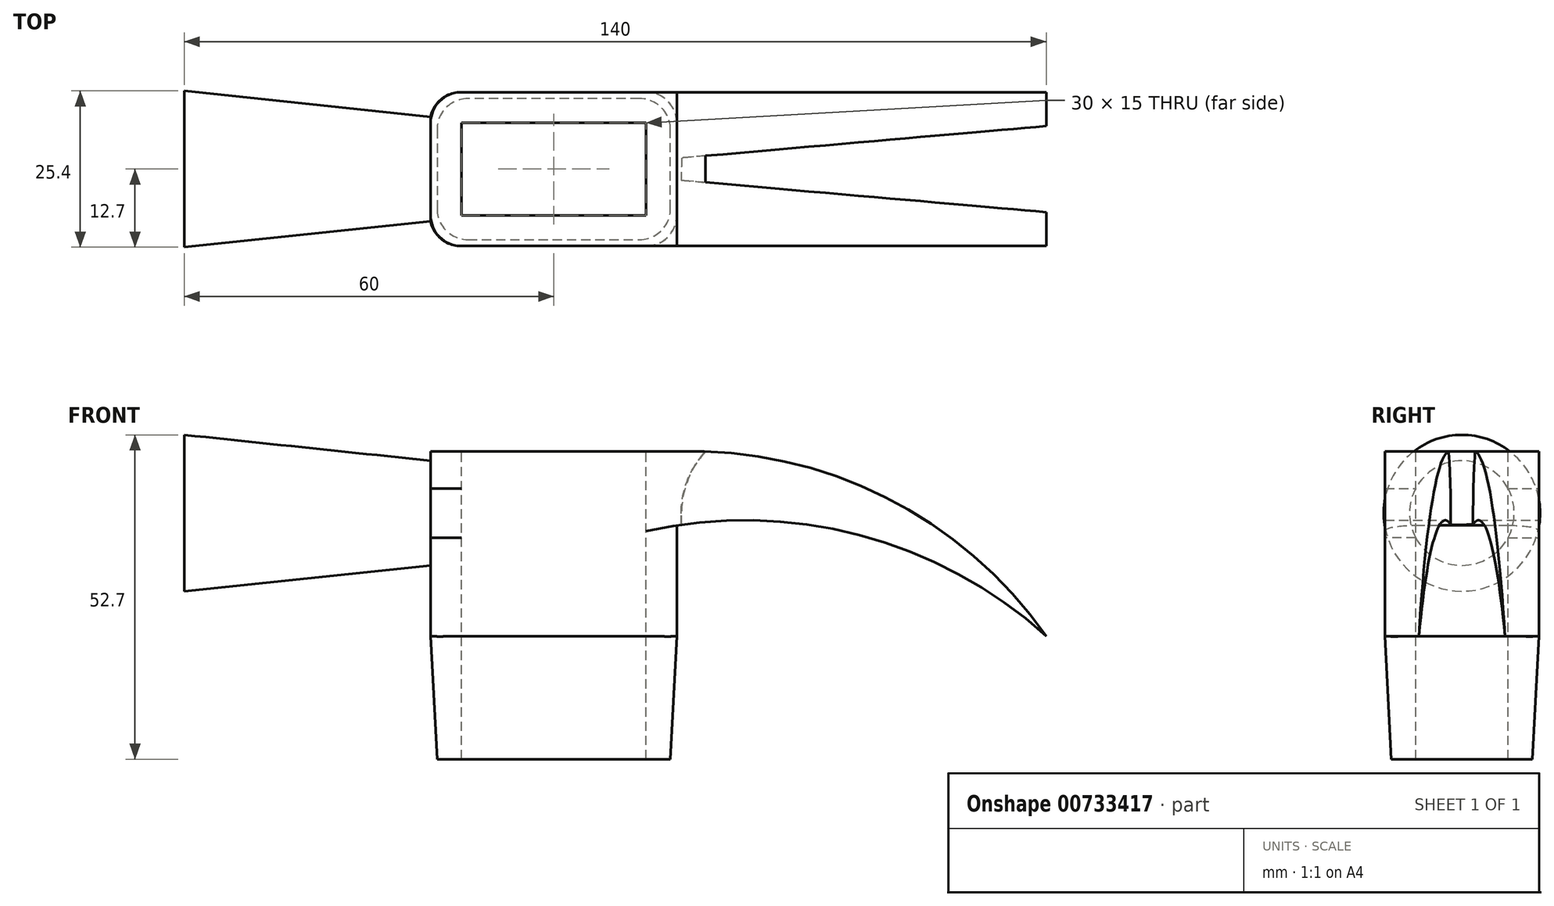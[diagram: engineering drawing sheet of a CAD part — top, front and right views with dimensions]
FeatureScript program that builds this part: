
annotation { "Feature Type Name" : "Feature", "Feature Type Description" : "" }
export const myFeature = defineFeature(function(context is Context, id is Id, definition is map)
    precondition{}
    {
        {
            var Q0;
            Q0=qCreatedBy(makeId("Front.planeOp"),FACE);
            var sketch = newSketch(context, id + "F0", { "sketchPlane" : qUnion([Q0])});
            skLineSegment(sketch, "E0.0", {"start": v(20, 0) * mm, "end": v(20, 30) * mm});
            skLineSegment(sketch, "E1.0", {"start": v(-20, 0) * mm, "end": v(-20, 30) * mm});
            skLineSegment(sketch, "E2", {"start": v(-20, 0) * mm, "end": v(20, 0) * mm});
            skLineSegment(sketch, "E3.0", {"start": v(-20, 30) * mm, "end": v(20, 30) * mm});
            skSolve(sketch);
        }
        {
            var Q0;
            Q0=makeQuery(id+"F0.imprint","IMPRINT",FACE,{"disambiguationData":[TD([[makeQuery(id+"F0.imprint","IMPRINT",EDGE,{"derivedFrom":sQuery(id+"F0.wireOp",EDGE,"E0.0")}),1.0]])]});
            extrude(context, id + "F1", {"entities" : qUnion([Q0]), "endBound" : BoundingType.SYMMETRIC, "depth" : 25 * mm, "offsetDistance" : 25 * mm});
        }
        {
            var Q0;
            Q0=makeQuery(id+"F1.opExtrude","SWEPT_FACE",FACE,{"disambiguationData":[OSD([sQuery(id+"F0.wireOp",EDGE,"E1.0")])]});
            var sketch = newSketch(context, id + "F2", { "sketchPlane" : qUnion([Q0])});
            skCircle(sketch, "E4", {"center": v(0, 20) * mm, "radius": 8.5 * mm});
            skSolve(sketch);
        }
        {
            var Q0;
            Q0 = qSketchRegion(id + "F2", true);
            extrude(context, id + "F3", {"entities" : qUnion([Q0]), "operationType" : NewBodyOperationType.ADD, "depth" : 40 * mm, "offsetDistance" : 25 * mm, "hasDraft" : true, "draftAngle" : 6 * degree});
        }
        {
            var Q0;
            Q0=qCreatedBy(makeId("Front.planeOp"),FACE);
            var sketch = newSketch(context, id + "F4", { "sketchPlane" : qUnion([Q0])});
            skLineSegment(sketch, "E5.0", {"start": v(20, 0) * mm, "end": v(20, 30) * mm});
            skArc(sketch, "E6", {"start": v(80, 0) * mm, "mid": v(53.8, 22.6) * mm, "end": v(20, 30) * mm});
            skArc(sketch, "E7", {"start": v(80, 0) * mm, "mid": v(52.03, 15.76) * mm, "end": v(20, 18) * mm});
            skSolve(sketch);
        }
        {
            var Q0;
            {var subQ0=sQuery(id+"F4.wireOp",EDGE,"E6");Q0=makeQuery(id+"F4.imprint","IMPRINT",FACE,{"disambiguationData":[TD([[makeQuery(id+"F4.imprint","IMPRINT",EDGE,{"derivedFrom":subQ0}),1.0]])]});}
            extrude(context, id + "F5", {"entities" : qUnion([Q0]), "operationType" : NewBodyOperationType.ADD, "endBound" : BoundingType.SYMMETRIC, "depth" : 25 * mm, "offsetDistance" : 25 * mm});
        }
        {
            var Q0;
            Q0=makeQuery(id+"F1.opExtrude","SWEPT_FACE",FACE,{"disambiguationData":[OSD([sQuery(id+"F0.wireOp",EDGE,"E2")])]});
            extrude(context, id + "F6", {"entities" : qUnion([Q0]), "operationType" : NewBodyOperationType.ADD, "depth" : 20 * mm, "offsetDistance" : 25 * mm, "hasDraft" : true, "draftAngle" : 3 * degree, "draftPullDirection" : true});
        }
        {
            var Q0;
            Q0=makeQuery(id+"F1.opExtrude","SWEPT_FACE",FACE,{"disambiguationData":[OSD([sQuery(id+"F0.wireOp",EDGE,"E3.0")])]});
            var sketch = newSketch(context, id + "F7", { "sketchPlane" : qUnion([Q0])});
            skPoint(sketch, "E8.endSnap0", {"position": v(20, 0) * mm});
            skLineSegment(sketch, "E9", {"start": v(20.76, 1.82) * mm, "end": v(93.19, 8.15) * mm});
            skLineSegment(sketch, "E10", {"start": v(20.7, -1.81) * mm, "end": v(92.9, -8.13) * mm});
            skLineSegment(sketch, "E11.0", {"start": v(20.7, -1.81) * mm, "end": v(20.76, 1.82) * mm});
            skLineSegment(sketch, "E12.0", {"start": v(92.9, -8.13) * mm, "end": v(93.19, 8.15) * mm});
            skSolve(sketch);
        }
        {
            var Q0;
            Q0=makeQuery(id+"F7.imprint","IMPRINT",FACE,{"disambiguationData":[TD([[makeQuery(id+"F7.imprint","IMPRINT",EDGE,{"derivedFrom":sQuery(id+"F7.wireOp",EDGE,"E9")}),-1.0]])]});
            extrude(context, id + "F8", {"entities" : qUnion([Q0]), "operationType" : NewBodyOperationType.REMOVE, "oppositeDirection" : true, "depth" : 40 * mm, "offsetDistance" : 25 * mm});
        }
        {
            var Q0;
            Q0=makeQuery(id+"F1.opExtrude","SWEPT_FACE",FACE,{"disambiguationData":[OSD([sQuery(id+"F0.wireOp",EDGE,"E3.0")])]});
            var sketch = newSketch(context, id + "F9", { "sketchPlane" : qUnion([Q0])});
            skLineSegment(sketch, "E13.bottom", {"start": v(15, -7.5) * mm, "end": v(-15, -7.5) * mm});
            skLineSegment(sketch, "E13.top", {"start": v(15, 7.5) * mm, "end": v(-15, 7.5) * mm});
            skLineSegment(sketch, "E13.left", {"start": v(15, -7.5) * mm, "end": v(15, 7.5) * mm});
            skLineSegment(sketch, "E13.right", {"start": v(-15, -7.5) * mm, "end": v(-15, 7.5) * mm});
            skPoint(sketch, "E13.middle", {"position": v(0, 0) * mm});
            skSolve(sketch);
        }
        {
            var Q0;
            Q0 = qSketchRegion(id + "F9", true);
            extrude(context, id + "F10", {"entities" : qUnion([Q0]), "operationType" : NewBodyOperationType.REMOVE, "endBound" : BoundingType.SYMMETRIC, "oppositeDirection" : true, "depth" : 130.8 * mm, "offsetDistance" : 25 * mm});
        }
        {
            var Q0;
            Q0=makeQuery(id+"F1.opExtrude","CAP_EDGE",EDGE,{"disambiguationData":[OSD([sQuery(id+"F0.wireOp",EDGE,"E0.0")])],"isStart":true});
            var Q1;
            {var subQ0=sQuery(id+"F0.wireOp",EDGE,"E2");var subQ1=sQuery(id+"F0.wireOp",EDGE,"E0.0");Q1=makeQuery(id+"F6.opExtrude","SWEPT_EDGE",EDGE,{"disambiguationData":[OSD([subQ1,subQ0]),TDD([makeQuery(id+"F1.opExtrude","CAP_VERTEX",VERTEX,{"disambiguationData":[OSD([subQ1,subQ0])],"isStart":true})])]});}
            var Q2;
            {var subQ0=sQuery(id+"F0.wireOp",EDGE,"E2");var subQ1=sQuery(id+"F0.wireOp",EDGE,"E0.0");Q2=makeQuery(id+"F6.opExtrude","SWEPT_EDGE",EDGE,{"disambiguationData":[OSD([subQ1,subQ0]),TDD([makeQuery(id+"F1.opExtrude","CAP_VERTEX",VERTEX,{"disambiguationData":[OSD([subQ1,subQ0])],"isStart":false})])]});}
            var Q3;
            Q3=makeQuery(id+"F1.opExtrude","CAP_EDGE",EDGE,{"disambiguationData":[OSD([sQuery(id+"F0.wireOp",EDGE,"E0.0")])],"isStart":false});
            var Q4;
            Q4=makeQuery(id+"F1.opExtrude","CAP_EDGE",EDGE,{"disambiguationData":[OSD([sQuery(id+"F0.wireOp",EDGE,"E1.0")])],"isStart":false});
            var Q5;
            {var subQ0=sQuery(id+"F0.wireOp",EDGE,"E2");var subQ1=sQuery(id+"F0.wireOp",EDGE,"E1.0");Q5=makeQuery(id+"F6.opExtrude","SWEPT_EDGE",EDGE,{"disambiguationData":[OSD([subQ1,subQ0]),TDD([makeQuery(id+"F1.opExtrude","CAP_VERTEX",VERTEX,{"disambiguationData":[OSD([subQ1,subQ0])],"isStart":false})])]});}
            var Q6;
            {var subQ0=sQuery(id+"F0.wireOp",EDGE,"E2");var subQ1=sQuery(id+"F0.wireOp",EDGE,"E1.0");Q6=makeQuery(id+"F6.opExtrude","SWEPT_EDGE",EDGE,{"disambiguationData":[OSD([subQ1,subQ0]),TDD([makeQuery(id+"F1.opExtrude","CAP_VERTEX",VERTEX,{"disambiguationData":[OSD([subQ1,subQ0])],"isStart":true})])]});}
            var Q7;
            Q7=makeQuery(id+"F1.opExtrude","CAP_EDGE",EDGE,{"disambiguationData":[OSD([sQuery(id+"F0.wireOp",EDGE,"E1.0")])],"isStart":true});
            fillet(context, id + "F11", {"entities" : qUnion([Q0, Q1, Q2, Q3, Q4, Q5, Q6, Q7]), "radius" : 5 * mm, "tangentPropagation" : true, "allowEdgeOverflow" : false});
        }
        {
            var Q0;
            Q0=makeQuery(id+"F8.boolean.opBoolean","COPY",EDGE,{"derivedFrom":makeQuery(id+"F8.opExtrude","CAP_EDGE",EDGE,{"disambiguationData":[OSD([sQuery(id+"F7.wireOp",EDGE,"E11.0")])],"isStart":true})});
            fillet(context, id + "F12", {"entities" : qUnion([Q0]), "radius" : 14.73 * mm, "tangentPropagation" : true, "allowEdgeOverflow" : false});
        }
    });
